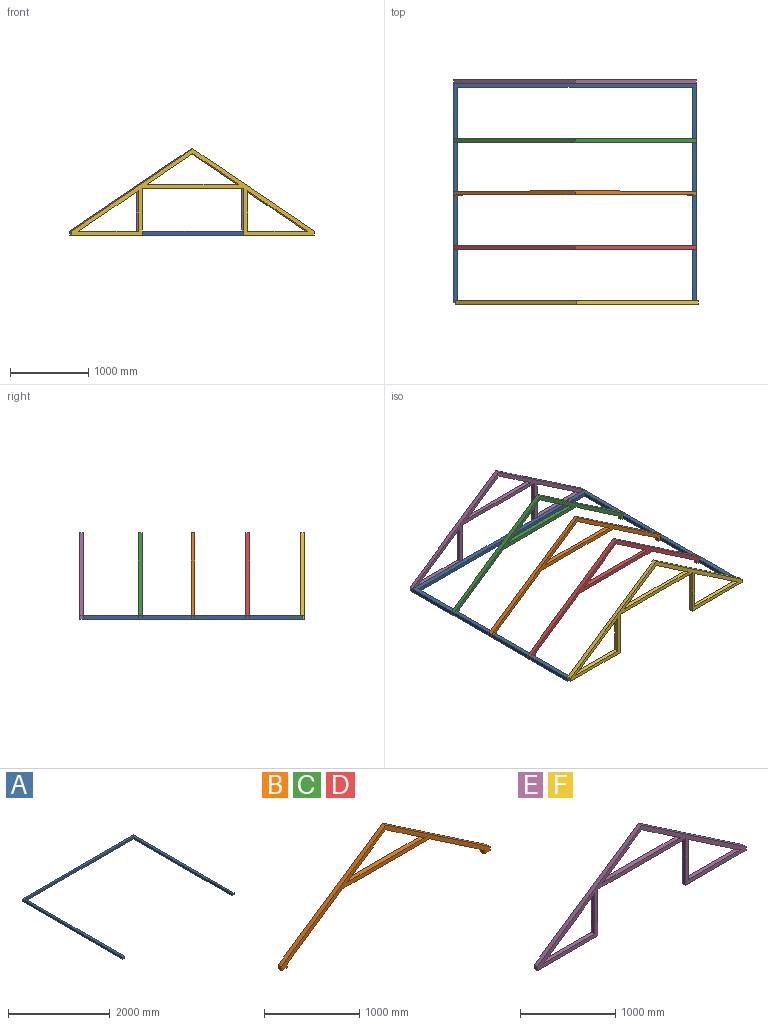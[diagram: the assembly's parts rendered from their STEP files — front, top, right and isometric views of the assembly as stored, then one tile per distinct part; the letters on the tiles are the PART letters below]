
ASSEMBLY  parts=6 mates=5
PART A: 10 faces, bbox 3100x2800x50 mm
  f0: plane 2800x50mm, normal (1,0,0), area 140000mm2, adj f1,f7,f8,f9
  f1: plane 3100x50mm, normal (0,1,0), area 155000mm2, adj f0,f2,f8,f9
  f2: plane 2800x50mm, normal (-1,0,0), area 140000mm2, adj f1,f3,f8,f9
  f3: plane 50x50mm, normal (0,-1,0), area 2500mm2, adj f2,f4,f8,f9
  f4: plane 2750x50mm, normal (1,0,0), area 137500mm2, adj f3,f5,f8,f9
  f5: plane 3000x50mm, normal (0,-1,0), area 150000mm2, adj f4,f6,f8,f9
  f6: plane 2750x50mm, normal (-1,0,0), area 137500mm2, adj f5,f7,f8,f9
  f7: plane 50x50mm, normal (0,-1,0), area 2500mm2, adj f0,f6,f8,f9
  f8: plane 3100x2800mm, normal (0,0,1), area 430000mm2, adj f0,f1,f2,f3,f4,f5,f6,f7
  f9: plane 3100x2800mm, normal (0,0,-1), area 430000mm2, adj f0,f1,f2,f3,f4,f5,f6,f7
PART B: 16 faces, bbox 3100x50x1101.3 mm
  f0: plane 1550x1051.27mm, normal (-0.56,0,0.83), area 93643.9mm2, adj f1,f13,f14,f15
  f1: plane 50x50mm, normal (-1,0,0), area 2500mm2, adj f0,f2,f14,f15
  f2: plane 89.08x50mm, normal (0,0,-1), area 4453.8mm2, adj f1,f3,f14,f15
  f3: plane 50x50mm, normal (1,0,0), area 2500mm2, adj f2,f4,f14,f15
  f4: plane 810.92x550mm, normal (0.56,0,-0.83), area 48992.3mm2, adj f3,f5,f14,f15
  f5: plane 1300x50mm, normal (0,0,-1), area 65000mm2, adj f4,f6,f14,f15
  f6: plane 810.92x550mm, normal (-0.56,0,-0.83), area 48992.3mm2, adj f5,f7,f14,f15
  f7: plane 50x50mm, normal (-1,0,0), area 2500mm2, adj f6,f8,f14,f15
  f8: plane 89.08x50mm, normal (0,0,-1), area 4453.8mm2, adj f7,f9,f14,f15
  f9: plane 50x50mm, normal (1,0,0), area 2500mm2, adj f8,f13,f14,f15
  f10: plane 1152.56x50mm, normal (0,0,1), area 57628mm2, adj f11,f12,f14,f15
  f11: plane 576.28x390.86mm, normal (0.56,0,-0.83), area 34816.2mm2, adj f10,f12,f14,f15
  f12: plane 576.28x390.86mm, normal (-0.56,0,-0.83), area 34816.2mm2, adj f10,f11,f14,f15
  f13: plane 1550x1051.27mm, normal (0.56,0,0.83), area 93643.9mm2, adj f0,f9,f14,f15
  f14: plane 3100x1101.27mm, normal (0,-1,0), area 252127.8mm2, adj f0,f1,f2,f3,f4,f5,f6,f7
  f15: plane 3100x1101.27mm, normal (0,1,0), area 252127.8mm2, adj f0,f1,f2,f3,f4,f5,f6,f7
PART C: same geometry as B
PART D: same geometry as B
PART E: 20 faces, bbox 3100x50x1101.3 mm
  f0: plane 516.09x50mm, normal (1,0,0), area 25804.4mm2, adj f1,f17,f18,f19
  f1: plane 760.92x516.09mm, normal (-0.56,0,-0.83), area 45971.5mm2, adj f0,f17,f18,f19
  f2: plane 760.92x516.09mm, normal (0.56,0,-0.83), area 45971.5mm2, adj f3,f14,f18,f19
  f3: plane 516.09x50mm, normal (-1,0,0), area 25804.4mm2, adj f2,f14,f18,f19
  f4: plane 1152.56x50mm, normal (0,0,1), area 57628mm2, adj f5,f15,f18,f19
  f5: plane 576.28x390.86mm, normal (0.56,0,-0.83), area 34816.2mm2, adj f4,f15,f18,f19
  f6: plane 600x50mm, normal (1,0,0), area 30000mm2, adj f7,f16,f18,f19
  f7: plane 1300x50mm, normal (0,0,-1), area 65000mm2, adj f6,f8,f18,f19
  f8: plane 600x50mm, normal (-1,0,0), area 30000mm2, adj f7,f9,f18,f19
  f9: plane 900x50mm, normal (0,0,-1), area 45000mm2, adj f8,f10,f18,f19
  f10: plane 50x50mm, normal (1,0,0), area 2500mm2, adj f9,f11,f18,f19
  f11: plane 1550x1051.27mm, normal (0.56,0,0.83), area 93643.9mm2, adj f10,f12,f18,f19
  f12: plane 1550x1051.27mm, normal (-0.56,0,0.83), area 93643.9mm2, adj f11,f13,f18,f19
  f13: plane 50x50mm, normal (-1,0,0), area 2500mm2, adj f12,f16,f18,f19
  f14: plane 760.92x50mm, normal (0,0,1), area 38046.2mm2, adj f2,f3,f18,f19
  f15: plane 576.28x390.86mm, normal (-0.56,0,-0.83), area 34816.2mm2, adj f4,f5,f18,f19
  f16: plane 900x50mm, normal (0,0,-1), area 45000mm2, adj f6,f13,f18,f19
  f17: plane 760.92x50mm, normal (0,0,1), area 38046.2mm2, adj f0,f1,f18,f19
  f18: plane 3100x1101.27mm, normal (0,-1,0), area 386524.5mm2, adj f0,f1,f2,f3,f4,f5,f6,f7
  f19: plane 3100x1101.27mm, normal (0,1,0), area 386524.5mm2, adj f0,f1,f2,f3,f4,f5,f6,f7
PART F: same geometry as E
PLACE A t=(625.21,949.64,528.56)mm
PLACE B rot(axis=(0,0,-1),180deg) t=(625.21,924.64,528.56)mm
PLACE C rot(axis=(0,0,-1),180deg) t=(625.21,1599.64,528.56)mm
PLACE D rot(axis=(0,0,1),180deg) t=(625.21,224.64,528.56)mm
PLACE E t=(625.21,2399.64,528.56)mm
PLACE F t=(650.21,-425.36,528.56)mm
MATE fastened A.f8 <-> E.f14  axis (0,0,1) through (-924.79,2349.64,578.56)mm
MATE fastened A.f9 <-> B.f8  axis (0,0,1) through (-924.79,949.64,528.56)mm
MATE fastened F.f16 <-> A.f9  axis (0,0,-1) through (-899.79,-450.36,528.56)mm
MATE fastened D.f8 <-> A.f9  axis (0,0,-1) through (-924.79,249.64,528.56)mm
MATE fastened C.f8 <-> A.f9  axis (0,0,-1) through (-924.79,1624.64,528.56)mm
